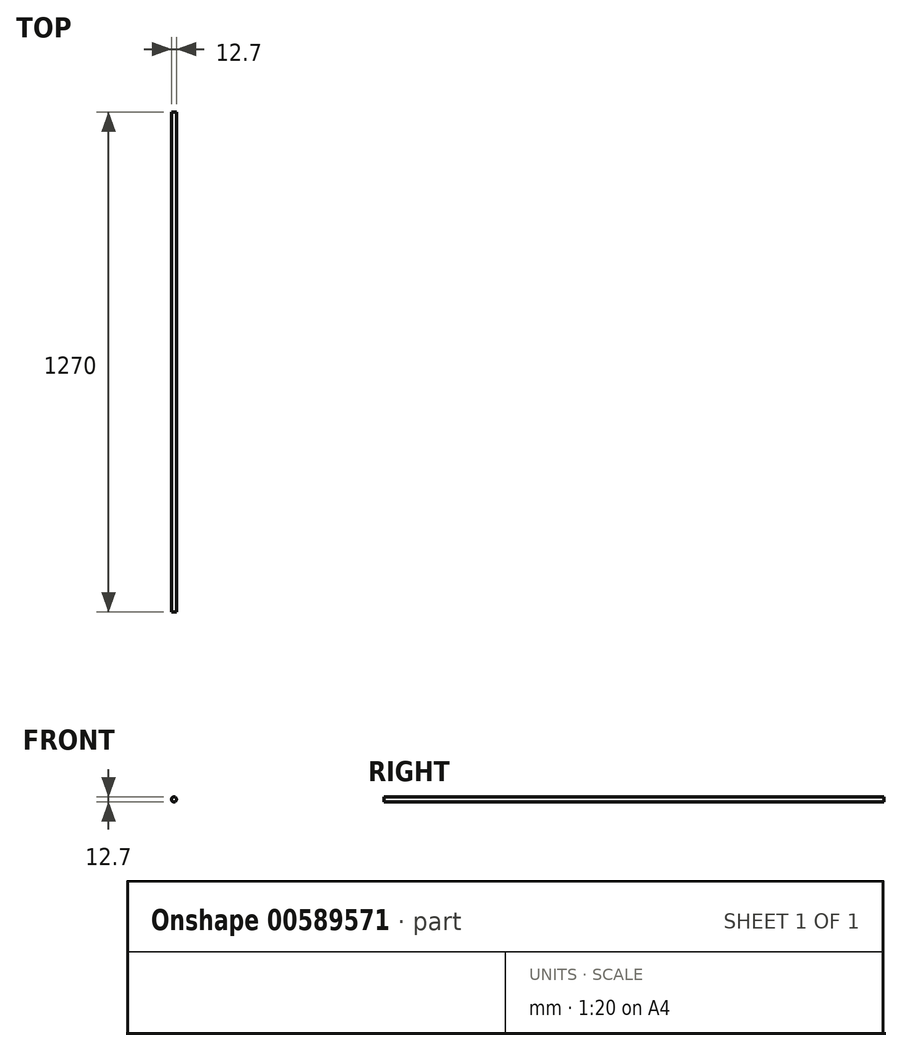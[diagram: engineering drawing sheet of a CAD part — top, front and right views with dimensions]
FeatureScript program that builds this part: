
annotation { "Feature Type Name" : "Feature", "Feature Type Description" : "" }
export const myFeature = defineFeature(function(context is Context, id is Id, definition is map)
    precondition{}
    {
        {
            var Q0;
            Q0=qCreatedBy(makeId("Front.planeOp"),FACE);
            var sketch = newSketch(context, id + "F0", { "sketchPlane" : qUnion([Q0])});
            skCircle(sketch, "E0", {"center": v(0, 0) * mm, "radius": 6.35 * mm});
            skSolve(sketch);
        }
        {
            var Q0;
            Q0=makeQuery(id+"F0.imprint","IMPRINT",FACE,{"disambiguationData":[TD([[makeQuery(id+"F0.imprint","IMPRINT",EDGE,{"derivedFrom":sQuery(id+"F0.wireOp",EDGE,"E0")}),1.0]])]});
            extrude(context, id + "F1", {"entities" : qUnion([Q0]), "depth" : 1270 * mm, "offsetDistance" : 25.4 * mm});
        }
    });
